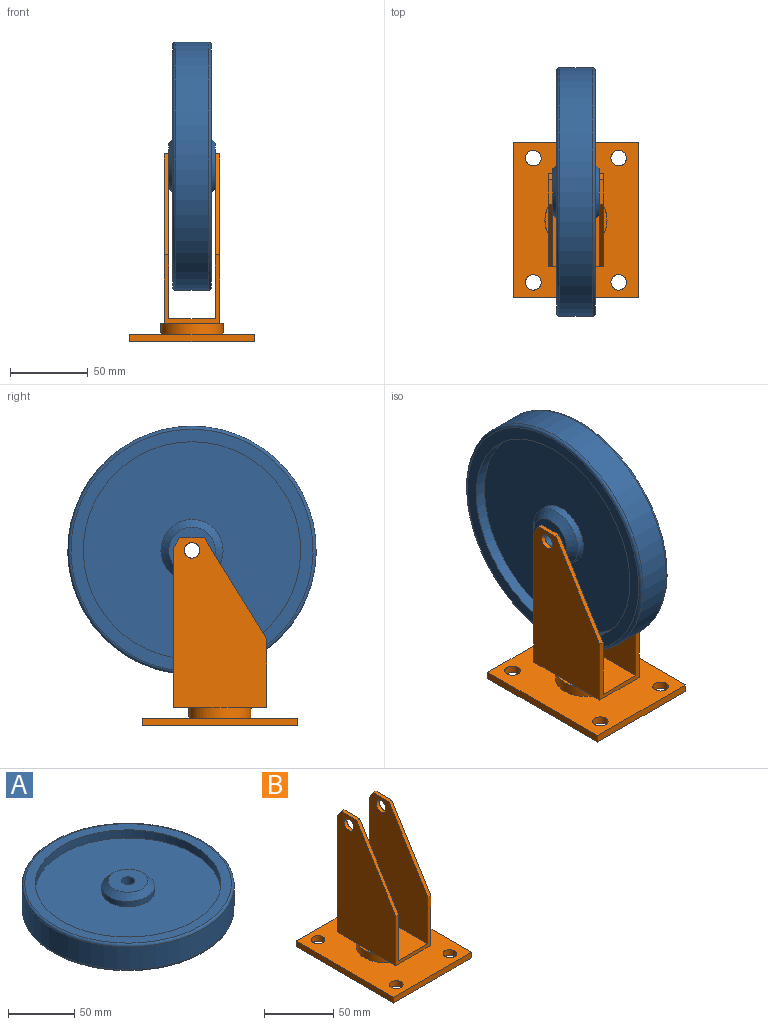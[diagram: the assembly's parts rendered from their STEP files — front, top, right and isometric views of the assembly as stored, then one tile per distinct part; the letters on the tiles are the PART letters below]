
ASSEMBLY  parts=2 mates=1
PART A: 16 faces, bbox 173.2x173.2x30 mm
  f0: cylinder r=20mm len=40mm, axis (0,0,-1), area 628.3mm2, adj f6,f14
  f1: cylinder r=5mm len=30mm, axis (0,0,-1), area 942.5mm2, adj f3,f4
  f2: cylinder r=20mm len=40mm, axis (0,0,-1), area 628.3mm2, adj f5,f15
  f3: plane 30x30mm, normal (0,0,1), area 628.3mm2, adj f1,f15
  f4: plane 30x30mm, normal (0,0,-1), area 628.3mm2, adj f1,f14
  f5: plane 140x140mm, normal (0,0,1), area 14137.2mm2, adj f2,f8
  f6: plane 140x140mm, normal (0,0,-1), area 14137.2mm2, adj f0,f7
  f7: cylinder r=70mm len=140mm, axis (0,0,-1), area 3298.7mm2, adj f6,f11
  f8: cylinder r=70mm len=140mm, axis (0,0,-1), area 3298.7mm2, adj f5,f10
  f9: cylinder r=80mm len=160mm, axis (0,0,-1), area 10555.8mm2, adj f12,f13
  f10: plane 156x156mm, normal (0,0,1), area 3719.6mm2, adj f8,f13
  f11: plane 156x156mm, normal (0,0,-1), area 3719.6mm2, adj f7,f12
  f12: torus R=78mm, axis (0,0,1), area 1564.8mm2, adj f9,f11
  f13: torus R=78mm, axis (0,0,1), area 1564.8mm2, adj f9,f10
  f14: cone r=20mm half-angle=45deg, axis (0,0,1), area 777.5mm2, adj f0,f4
  f15: cone r=15mm half-angle=45deg, axis (0,0,-1), area 777.5mm2, adj f2,f3
PART B: 30 faces, bbox 80x100x121 mm
  f0: plane 60x30mm, normal (0,0,1), area 1800mm2, adj f16,f18,f20,f22
  f1: plane 17.44x2mm, normal (0,0,1), area 23.5mm2, adj f12,f19
  f2: plane 80x5mm, normal (0,-1,0), area 400mm2, adj f3,f9,f10,f11
  f3: plane 100x5mm, normal (1,0,0), area 500mm2, adj f2,f4,f10,f11
  f4: plane 80x5mm, normal (0,1,0), area 400mm2, adj f3,f9,f10,f11
  f5: cylinder r=5mm len=10mm, axis (0,0,-1), area 157.1mm2, adj f10,f11
  f6: cylinder r=5mm len=10mm, axis (0,0,-1), area 157.1mm2, adj f10,f11
  f7: cylinder r=5mm len=10mm, axis (0,0,-1), area 157.1mm2, adj f10,f11
  f8: cylinder r=5mm len=10mm, axis (0,0,-1), area 157.1mm2, adj f10,f11
  f9: plane 100x5mm, normal (-1,0,0), area 500mm2, adj f2,f4,f10,f11
  f10: plane 100x80mm, normal (0,0,1), area 6429.2mm2, adj f2,f3,f4,f5,f6,f7,f8,f9
  f11: plane 100x80mm, normal (0,0,-1), area 7685.8mm2, adj f2,f3,f4,f5,f6,f7,f8,f9
  f12: cylinder r=20mm len=40mm, axis (0,0,-1), area 879.6mm2, adj f1,f10,f13,f14,f15
  f13: plane 17.44x2mm, normal (0,0,1), area 23.5mm2, adj f12,f17
  f14: plane 36x21.28mm, normal (0,0,-1), area 475.2mm2, adj f12,f17,f18,f19
  f15: plane 36x21.28mm, normal (0,0,-1), area 475.2mm2, adj f12,f16,f17,f19
  f16: plane 44x36mm, normal (0,-1,0), area 354mm2, adj f0,f15,f17,f19,f20,f22,f24,f25
  f17: plane 109x60mm, normal (1,0,0), area 5148.5mm2, adj f13,f14,f15,f16,f18,f23,f25,f27
  f18: plane 102.5x36mm, normal (0,1,0), area 705mm2, adj f0,f14,f17,f19,f20,f22,f26,f27
  f19: plane 109x60mm, normal (-1,0,0), area 5148.5mm2, adj f1,f14,f15,f16,f18,f21,f24,f26
  f20: plane 106x60mm, normal (1,0,0), area 4968.5mm2, adj f0,f16,f18,f21,f24,f26,f29
  f21: plane 16x3mm, normal (0,0,1), area 48mm2, adj f19,f20,f24,f26
  f22: plane 106x60mm, normal (-1,0,0), area 4968.5mm2, adj f0,f16,f18,f23,f25,f27,f28
  f23: plane 16x3mm, normal (0,0,1), area 48mm2, adj f17,f22,f25,f27
  f24: plane 65x40mm, normal (0,-0.85,0.52), area 229mm2, adj f16,f19,f20,f21
  f25: plane 65x40mm, normal (0,-0.85,0.52), area 229mm2, adj f16,f17,f22,f23
  f26: plane 6.5x4mm, normal (0,0.85,0.52), area 22.9mm2, adj f18,f19,f20,f21
  f27: plane 6.5x4mm, normal (0,0.85,0.52), area 22.9mm2, adj f17,f18,f22,f23
  f28: cylinder r=5mm len=10mm, axis (-1,0,0), area 94.2mm2, adj f17,f22
  f29: cylinder r=5mm len=10mm, axis (-1,0,0), area 94.2mm2, adj f19,f20
PLACE A rot(axis=(0,-1,0),90deg) t=(-83.7,-2.04,62.69)mm
PLACE B t=(-83.7,-20.04,-50.31)mm
MATE revolute A.f0 <-> B.f28  axis (-1,0,0) through (-98.7,-2.04,62.69)mm
